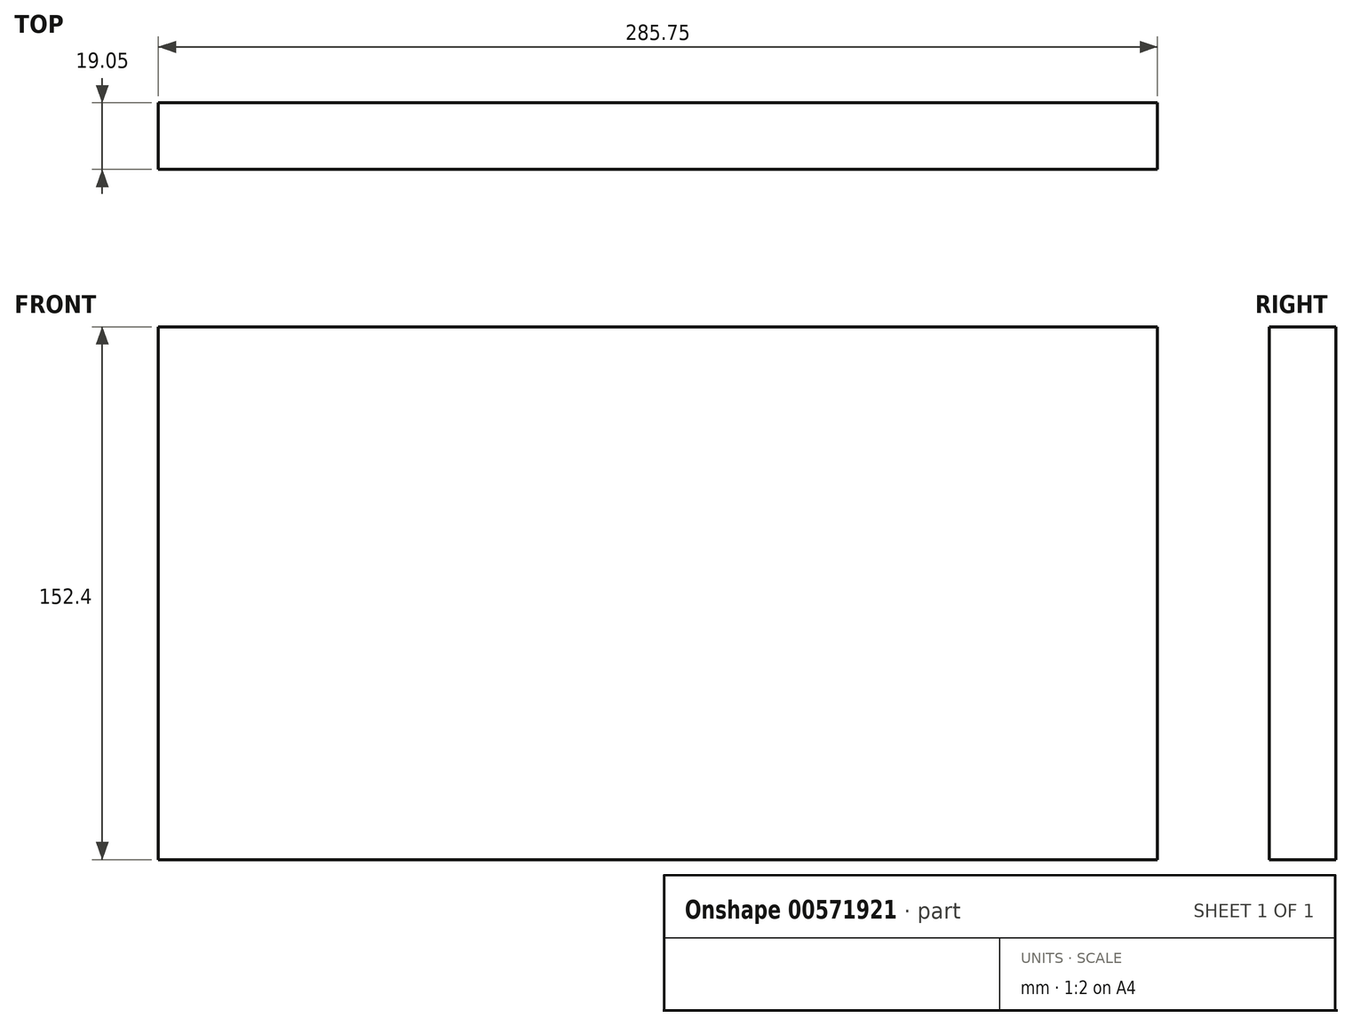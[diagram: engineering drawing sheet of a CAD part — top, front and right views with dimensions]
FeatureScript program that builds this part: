
annotation { "Feature Type Name" : "Feature", "Feature Type Description" : "" }
export const myFeature = defineFeature(function(context is Context, id is Id, definition is map)
    precondition{}
    {
        {
            var Q0;
            Q0=qCreatedBy(makeId("Top.planeOp"),FACE);
            var sketch = newSketch(context, id + "F0", { "sketchPlane" : qUnion([Q0])});
            skLineSegment(sketch, "E0", {"start": v(-129.66, -38.99) * mm, "end": v(156.1, -38.99) * mm});
            skLineSegment(sketch, "E1", {"start": v(156.1, -38.99) * mm, "end": v(156.1, -19.94) * mm});
            skLineSegment(sketch, "E2", {"start": v(156.1, -19.94) * mm, "end": v(-129.66, -19.94) * mm});
            skLineSegment(sketch, "E3", {"start": v(-129.66, -19.94) * mm, "end": v(-129.66, -38.99) * mm});
            skSolve(sketch);
        }
        {
            var Q0;
            Q0 = qSketchRegion(id + "F0", true);
            extrude(context, id + "F1", {"entities" : qUnion([Q0]), "depth" : 152.4 * mm, "offsetDistance" : 25.4 * mm});
        }
    });
